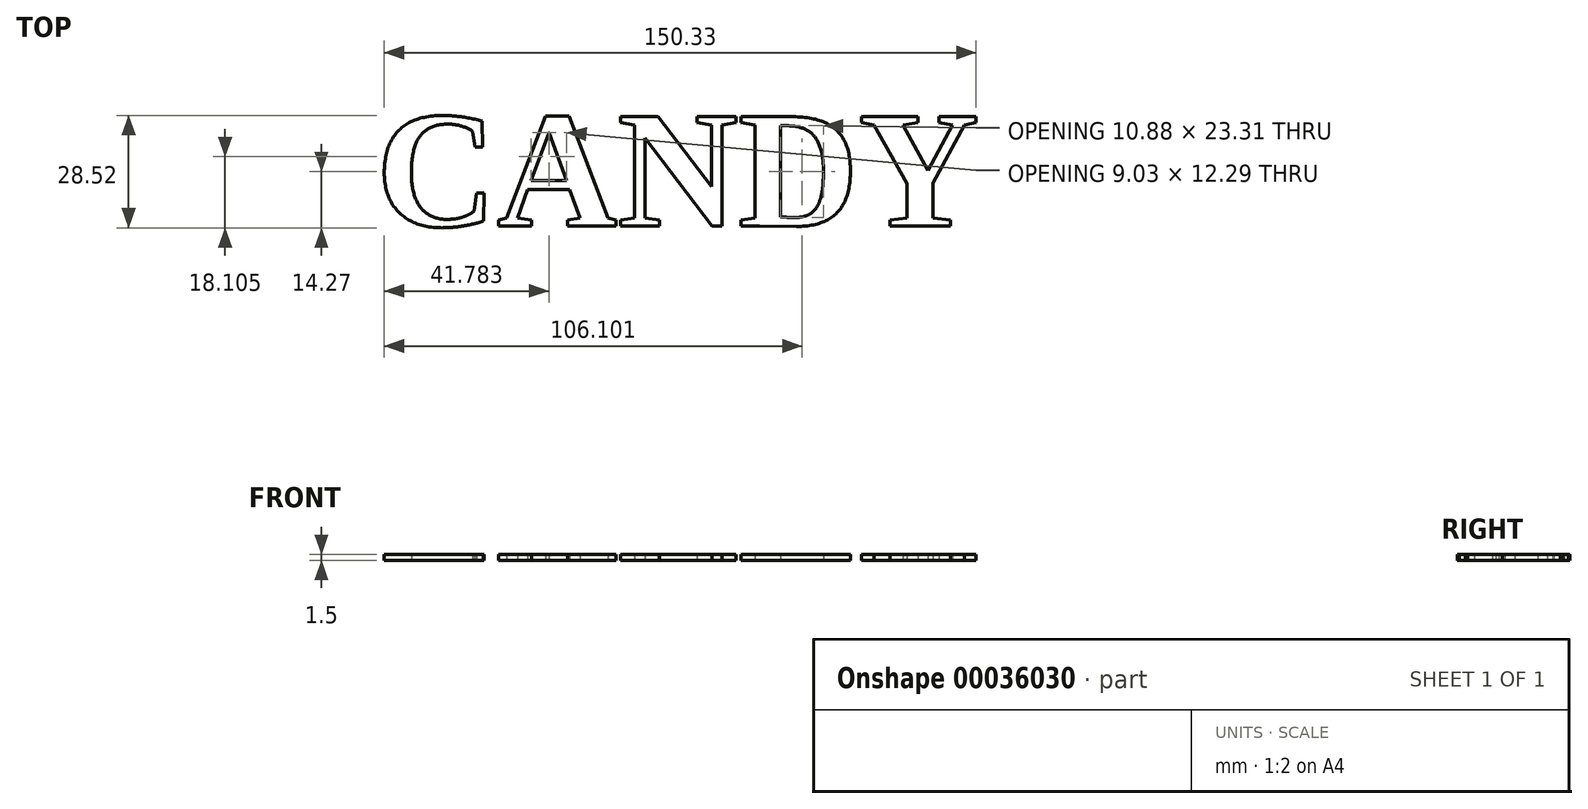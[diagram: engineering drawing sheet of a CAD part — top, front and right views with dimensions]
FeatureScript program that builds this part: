
annotation { "Feature Type Name" : "Feature", "Feature Type Description" : "" }
export const myFeature = defineFeature(function(context is Context, id is Id, definition is map)
    precondition{}
    {
        {
            var Q0;
            Q0=qCreatedBy(makeId("Top.planeOp"),FACE);
            var sketch = newSketch(context, id + "F0", { "sketchPlane" : qUnion([Q0])});
            skText(sketch, "E0", { "text": "CANDY", "fontName": "Tinos-Bold.ttf"});
            const initialGuessF0  = {"E0": [-0.07488, -0.01372, 1, 0, 0.03055]};
            skSetInitialGuess(sketch, initialGuessF0);
            skSolve(sketch);
        }
        {
            var Q0;
            Q0 = qSketchRegion(id + "F0", true);
            extrude(context, id + "F1", {"entities" : qUnion([Q0]), "depth" : 1.5 * mm});
        }
    });
